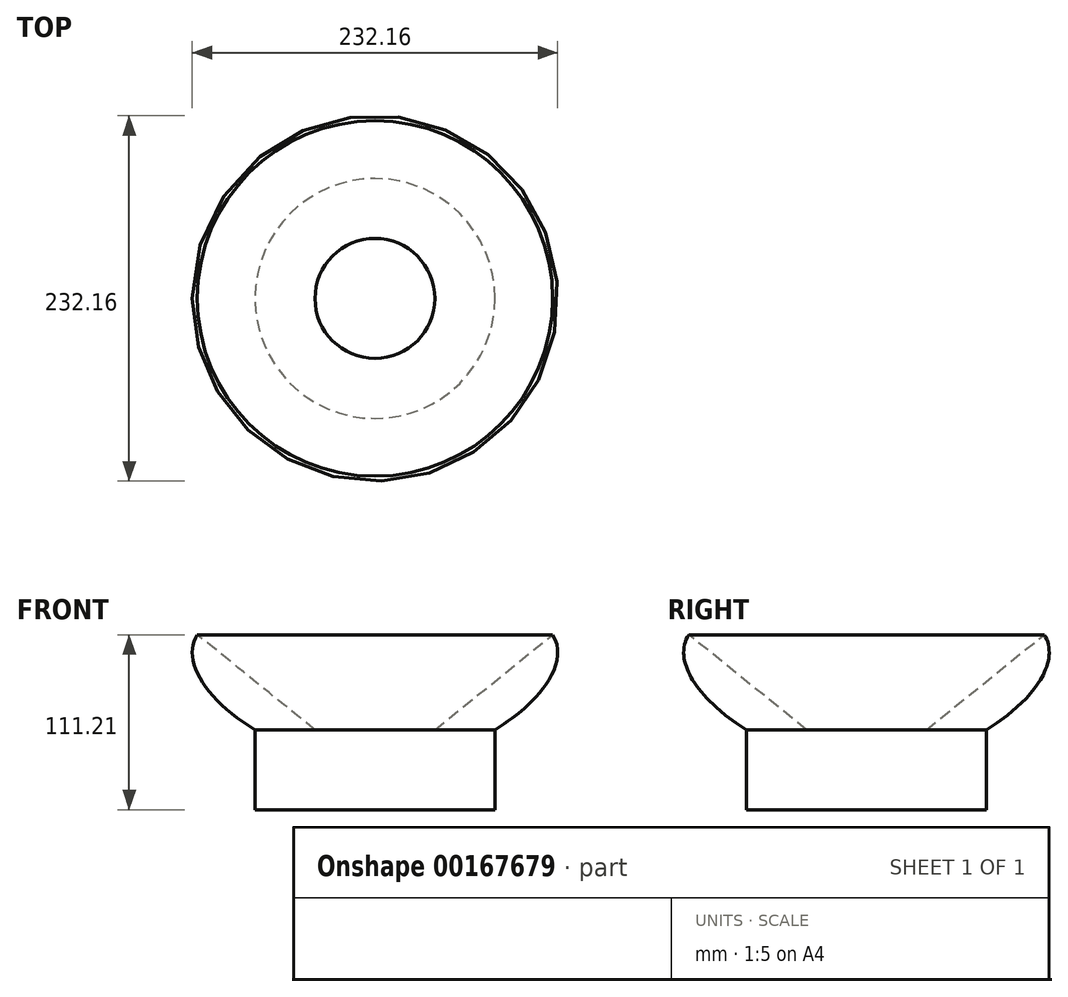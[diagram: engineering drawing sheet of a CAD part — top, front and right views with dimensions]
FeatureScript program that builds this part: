
annotation { "Feature Type Name" : "Feature", "Feature Type Description" : "" }
export const myFeature = defineFeature(function(context is Context, id is Id, definition is map)
    precondition{}
    {
        {
            var Q0;
            Q0=qCreatedBy(makeId("Front.planeOp"),FACE);
            var sketch = newSketch(context, id + "F0", { "sketchPlane" : qUnion([Q0])});
            skLineSegment(sketch, "E0.bottom", {"start": v(0, 0) * mm, "end": v(76.2, 0) * mm});
            skLineSegment(sketch, "E0.top", {"start": v(0, 50.8) * mm, "end": v(38.1, 50.8) * mm});
            skLineSegment(sketch, "E0.left", {"start": v(0, 0) * mm, "end": v(0, 50.8) * mm});
            skLineSegment(sketch, "E0.right", {"start": v(76.2, 0) * mm, "end": v(76.2, 50.8) * mm});
            skEllipticalArc(sketch, "E1", {});
            skPoint(sketch, "E1.centerSnap0", {"position": v(38.1, 50.8) * mm});
            skLineSegment(sketch, "E2", {"start": v(112.89, 111.21) * mm, "end": v(38.1, 50.8) * mm});
            skPoint(sketch, "E3", {"position": v(-107.65, 30.92) * mm});
            skLineSegment(sketch, "E4.bottom", {"start": v(-56.05, 48.86) * mm, "end": v(-28.83, 48.86) * mm});
            skLineSegment(sketch, "E4.top", {"start": v(-56.05, 8.97) * mm, "end": v(-28.83, 8.97) * mm});
            skLineSegment(sketch, "E4.left", {"start": v(-56.05, 48.86) * mm, "end": v(-56.05, 8.97) * mm});
            skLineSegment(sketch, "E4.right", {"start": v(-28.83, 48.86) * mm, "end": v(-28.83, 8.97) * mm});
            skLineSegment(sketch, "E5", {"start": v(-45.07, 39.78) * mm, "end": v(-39.34, 21.4) * mm});
            skLineSegment(sketch, "E6", {"start": v(-39.34, 21.4) * mm, "end": v(-47.22, 17.1) * mm});
            skLineSegment(sketch, "E7", {"start": v(-47.22, 17.1) * mm, "end": v(-56.05, 37.87) * mm});
            skLineSegment(sketch, "E8", {"start": v(-56.05, 37.87) * mm, "end": v(-45.07, 39.78) * mm});
            const initialGuessF0  = {"E1": [0.0381, 0.07629290223121643, 0.9234210031057075, 0.3837885498855443, 0.082783350969383, 0.040096815701457754, 5.024224692487634, 0.0884424541818468]};
            skSetInitialGuess(sketch, initialGuessF0);
            skSolve(sketch);
        }
        {
            var Q0;
            Q0=makeQuery(id+"F0.imprint","IMPRINT",FACE,{"disambiguationData":[TD([[makeQuery(id+"F0.imprint","IMPRINT",EDGE,{"derivedFrom":sQuery(id+"F0.wireOp",EDGE,"E0.bottom")}),1.0]])]});
            var Q1;
            Q1=sQuery(id+"F0.wireOp",EDGE,"E0.left");
            revolve(context, id + "F1", {"entities" : qUnion([Q0]), "axis" : qUnion([Q1]), "revolveType" : RevolveType.FULL});
        }
    });
